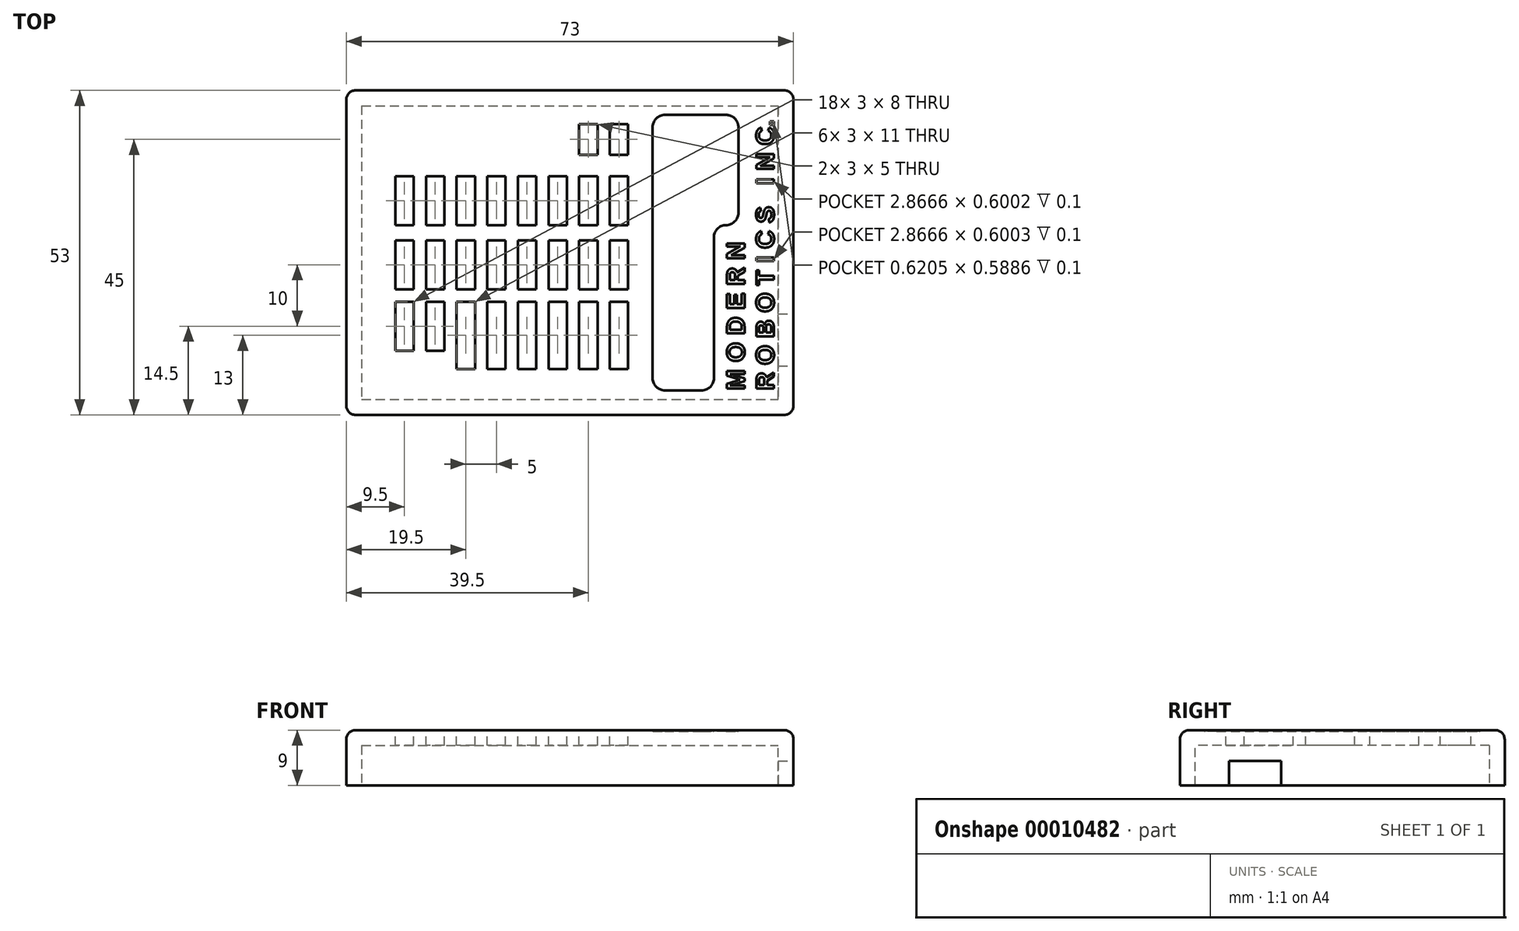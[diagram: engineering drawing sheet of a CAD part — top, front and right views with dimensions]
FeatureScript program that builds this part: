
annotation { "Feature Type Name" : "Feature", "Feature Type Description" : "" }
export const myFeature = defineFeature(function(context is Context, id is Id, definition is map)
    precondition{}
    {
        {
            var Q0;
            Q0=qCreatedBy(makeId("Top.planeOp"),FACE);
            var sketch = newSketch(context, id + "F0", { "sketchPlane" : qUnion([Q0])});
            skLineSegment(sketch, "E0.bottom", {"start": v(0, 0) * mm, "end": v(73, 0) * mm});
            skLineSegment(sketch, "E0.top", {"start": v(0, 53) * mm, "end": v(73, 53) * mm});
            skLineSegment(sketch, "E0.left", {"start": v(0, 0) * mm, "end": v(0, 53) * mm});
            skLineSegment(sketch, "E0.right", {"start": v(73, 0) * mm, "end": v(73, 53) * mm});
            skSolve(sketch);
        }
        {
            var Q0;
            Q0=qSketchRegion(id+"F0",true);
            extrude(context, id + "F1", {"entities" : qUnion([Q0]), "depth" : 9 * mm});
        }
        {
            var Q0;
            Q0=makeQuery(id+"F1.opExtrude","SWEPT_EDGE",EDGE,{"disambiguationData":[OSD([sQuery(id+"F0.wireOp",EDGE,"E0.bottom"),sQuery(id+"F0.wireOp",EDGE,"E0.left")])]});
            var Q1;
            Q1=makeQuery(id+"F1.opExtrude","CAP_EDGE",EDGE,{"disambiguationData":[OSD([sQuery(id+"F0.wireOp",EDGE,"E0.bottom")])],"isStart":false});
            var Q2;
            Q2=makeQuery(id+"F1.opExtrude","CAP_EDGE",EDGE,{"disambiguationData":[OSD([sQuery(id+"F0.wireOp",EDGE,"E0.left")])],"isStart":false});
            var Q3;
            Q3=makeQuery(id+"F1.opExtrude","SWEPT_EDGE",EDGE,{"disambiguationData":[OSD([sQuery(id+"F0.wireOp",EDGE,"E0.bottom"),sQuery(id+"F0.wireOp",EDGE,"E0.right")])]});
            var Q4;
            Q4=makeQuery(id+"F1.opExtrude","CAP_EDGE",EDGE,{"disambiguationData":[OSD([sQuery(id+"F0.wireOp",EDGE,"E0.right")])],"isStart":false});
            var Q5;
            Q5=makeQuery(id+"F1.opExtrude","CAP_EDGE",EDGE,{"disambiguationData":[OSD([sQuery(id+"F0.wireOp",EDGE,"E0.top")])],"isStart":false});
            var Q6;
            Q6=makeQuery(id+"F1.opExtrude","SWEPT_EDGE",EDGE,{"disambiguationData":[OSD([sQuery(id+"F0.wireOp",EDGE,"E0.top"),sQuery(id+"F0.wireOp",EDGE,"E0.right")])]});
            var Q7;
            Q7=makeQuery(id+"F1.opExtrude","SWEPT_EDGE",EDGE,{"disambiguationData":[OSD([sQuery(id+"F0.wireOp",EDGE,"E0.top"),sQuery(id+"F0.wireOp",EDGE,"E0.left")])]});
            fillet(context, id + "F2", {"entities" : qUnion([Q0, Q1, Q2, Q3, Q4, Q5, Q6, Q7]), "radius" : 1.5 * mm, "tangentPropagation" : true, "allowEdgeOverflow" : false});
        }
        {
            var Q0;
            Q0=makeQuery(id+"F1.opExtrude","CAP_FACE",FACE,{"disambiguationData":[OSD([sQuery(id+"F0.wireOp",EDGE,"E0.bottom"),sQuery(id+"F0.wireOp",EDGE,"E0.top"),sQuery(id+"F0.wireOp",EDGE,"E0.left"),sQuery(id+"F0.wireOp",EDGE,"E0.right")])],"isStart":true});
            shell(context, id + "F3", {"entities" : qUnion([Q0]), "thickness" : 2.5 * mm});
        }
        {
            var Q0;
            Q0=makeQuery(id+"F1.opExtrude","SWEPT_FACE",FACE,{"disambiguationData":[OSD([sQuery(id+"F0.wireOp",EDGE,"E0.right")])]});
            var sketch = newSketch(context, id + "F4", { "sketchPlane" : qUnion([Q0])});
            skLineSegment(sketch, "E1.bottom", {"start": v(8, 4) * mm, "end": v(16.5, 4) * mm});
            skLineSegment(sketch, "E1.top", {"start": v(8, 0) * mm, "end": v(16.5, 0) * mm});
            skLineSegment(sketch, "E1.left", {"start": v(8, 4) * mm, "end": v(8, 0) * mm});
            skLineSegment(sketch, "E1.right", {"start": v(16.5, 4) * mm, "end": v(16.5, 0) * mm});
            skPoint(sketch, "E2", {"position": v(16.97, -0.37) * mm});
            skPoint(sketch, "E3", {"position": v(100.9, 31.9) * mm});
            skSolve(sketch);
        }
        {
            var Q0;
            Q0=qSketchRegion(id+"F4",true);
            extrude(context, id + "F5", {"entities" : qUnion([Q0]), "operationType" : NewBodyOperationType.REMOVE, "endBound" : BoundingType.UP_TO_NEXT, "oppositeDirection" : true, "depth" : 25 * mm});
        }
        {
            var Q0;
            Q0=makeQuery(id+"F1.opExtrude","CAP_FACE",FACE,{"disambiguationData":[OSD([sQuery(id+"F0.wireOp",EDGE,"E0.bottom"),sQuery(id+"F0.wireOp",EDGE,"E0.top"),sQuery(id+"F0.wireOp",EDGE,"E0.left"),sQuery(id+"F0.wireOp",EDGE,"E0.right")])],"isStart":false});
            var sketch = newSketch(context, id + "F6", { "sketchPlane" : qUnion([Q0])});
            skText(sketch, "E4", { "text": "M O D E R N\nR O B O T I C S   I N C.", "fontName": "Arimo-Bold.ttf"});
            const initialGuessF6  = {"E4": [0.065, 0.004, 0, 1, 0.003]};
            skSetInitialGuess(sketch, initialGuessF6);
            skSolve(sketch);
        }
        {
            var Q0;
            Q0=qSketchRegion(id+"F6",true);
            extrude(context, id + "F7", {"entities" : qUnion([Q0]), "operationType" : NewBodyOperationType.REMOVE, "oppositeDirection" : true, "depth" : .1 * mm});
        }
        {
            var Q0;
            Q0=makeQuery(id+"F6.imprint","IMPRINT",FACE,{"disambiguationData":[TD([[makeQuery(id+"F6.imprint","IMPRINT",EDGE,{"derivedFrom":sQuery(id+"F6.wireOp",EDGE,"E4.sketch_text.stroke-0")}),1.0]])]});
            var sketch = newSketch(context, id + "F8", { "sketchPlane" : qUnion([Q0])});
            skLineSegment(sketch, "E5.bottom", {"start": v(8, 31) * mm, "end": v(11, 31) * mm});
            skLineSegment(sketch, "E5.top", {"start": v(8, 39) * mm, "end": v(11, 39) * mm});
            skLineSegment(sketch, "E5.left", {"start": v(8, 31) * mm, "end": v(8, 39) * mm});
            skLineSegment(sketch, "E5.right", {"start": v(11, 31) * mm, "end": v(11, 39) * mm});
            skLineSegment(sketch, "E6.0.1.0", {"start": v(8, 20.5) * mm, "end": v(8, 28.5) * mm});
            skLineSegment(sketch, "E6.0.1.1", {"start": v(11, 20.5) * mm, "end": v(11, 28.5) * mm});
            skLineSegment(sketch, "E6.0.1.2", {"start": v(8, 20.5) * mm, "end": v(11, 20.5) * mm});
            skLineSegment(sketch, "E6.0.1.3", {"start": v(8, 28.5) * mm, "end": v(11, 28.5) * mm});
            skLineSegment(sketch, "E6.1.0.0", {"start": v(13, 31) * mm, "end": v(13, 39) * mm});
            skLineSegment(sketch, "E6.1.0.1", {"start": v(16, 31) * mm, "end": v(16, 39) * mm});
            skLineSegment(sketch, "E6.1.0.2", {"start": v(13, 31) * mm, "end": v(16, 31) * mm});
            skLineSegment(sketch, "E6.1.0.3", {"start": v(13, 39) * mm, "end": v(16, 39) * mm});
            skLineSegment(sketch, "E6.1.1.0", {"start": v(13, 20.5) * mm, "end": v(13, 28.5) * mm});
            skLineSegment(sketch, "E6.1.1.1", {"start": v(16, 20.5) * mm, "end": v(16, 28.5) * mm});
            skLineSegment(sketch, "E6.1.1.2", {"start": v(13, 20.5) * mm, "end": v(16, 20.5) * mm});
            skLineSegment(sketch, "E6.1.1.3", {"start": v(13, 28.5) * mm, "end": v(16, 28.5) * mm});
            skLineSegment(sketch, "E6.2.0.0", {"start": v(18, 31) * mm, "end": v(18, 39) * mm});
            skLineSegment(sketch, "E6.2.0.1", {"start": v(21, 31) * mm, "end": v(21, 39) * mm});
            skLineSegment(sketch, "E6.2.0.2", {"start": v(18, 31) * mm, "end": v(21, 31) * mm});
            skLineSegment(sketch, "E6.2.0.3", {"start": v(18, 39) * mm, "end": v(21, 39) * mm});
            skLineSegment(sketch, "E6.2.1.0", {"start": v(18, 20.5) * mm, "end": v(18, 28.5) * mm});
            skLineSegment(sketch, "E6.2.1.1", {"start": v(21, 20.5) * mm, "end": v(21, 28.5) * mm});
            skLineSegment(sketch, "E6.2.1.2", {"start": v(18, 20.5) * mm, "end": v(21, 20.5) * mm});
            skLineSegment(sketch, "E6.2.1.3", {"start": v(18, 28.5) * mm, "end": v(21, 28.5) * mm});
            skLineSegment(sketch, "E6.3.0.0", {"start": v(23, 31) * mm, "end": v(23, 39) * mm});
            skLineSegment(sketch, "E6.3.0.1", {"start": v(26, 31) * mm, "end": v(26, 39) * mm});
            skLineSegment(sketch, "E6.3.0.2", {"start": v(23, 31) * mm, "end": v(26, 31) * mm});
            skLineSegment(sketch, "E6.3.0.3", {"start": v(23, 39) * mm, "end": v(26, 39) * mm});
            skLineSegment(sketch, "E6.3.1.0", {"start": v(23, 20.5) * mm, "end": v(23, 28.5) * mm});
            skLineSegment(sketch, "E6.3.1.1", {"start": v(26, 20.5) * mm, "end": v(26, 28.5) * mm});
            skLineSegment(sketch, "E6.3.1.2", {"start": v(23, 20.5) * mm, "end": v(26, 20.5) * mm});
            skLineSegment(sketch, "E6.3.1.3", {"start": v(23, 28.5) * mm, "end": v(26, 28.5) * mm});
            skLineSegment(sketch, "E6.4.0.0", {"start": v(28, 31) * mm, "end": v(28, 39) * mm});
            skLineSegment(sketch, "E6.4.0.1", {"start": v(31, 31) * mm, "end": v(31, 39) * mm});
            skLineSegment(sketch, "E6.4.0.2", {"start": v(28, 31) * mm, "end": v(31, 31) * mm});
            skLineSegment(sketch, "E6.4.0.3", {"start": v(28, 39) * mm, "end": v(31, 39) * mm});
            skLineSegment(sketch, "E6.4.1.0", {"start": v(28, 20.5) * mm, "end": v(28, 28.5) * mm});
            skLineSegment(sketch, "E6.4.1.1", {"start": v(31, 20.5) * mm, "end": v(31, 28.5) * mm});
            skLineSegment(sketch, "E6.4.1.2", {"start": v(28, 20.5) * mm, "end": v(31, 20.5) * mm});
            skLineSegment(sketch, "E6.4.1.3", {"start": v(28, 28.5) * mm, "end": v(31, 28.5) * mm});
            skLineSegment(sketch, "E6.5.0.0", {"start": v(33, 31) * mm, "end": v(33, 39) * mm});
            skLineSegment(sketch, "E6.5.0.1", {"start": v(36, 31) * mm, "end": v(36, 39) * mm});
            skLineSegment(sketch, "E6.5.0.2", {"start": v(33, 31) * mm, "end": v(36, 31) * mm});
            skLineSegment(sketch, "E6.5.0.3", {"start": v(33, 39) * mm, "end": v(36, 39) * mm});
            skLineSegment(sketch, "E6.5.1.0", {"start": v(33, 20.5) * mm, "end": v(33, 28.5) * mm});
            skLineSegment(sketch, "E6.5.1.1", {"start": v(36, 20.5) * mm, "end": v(36, 28.5) * mm});
            skLineSegment(sketch, "E6.5.1.2", {"start": v(33, 20.5) * mm, "end": v(36, 20.5) * mm});
            skLineSegment(sketch, "E6.5.1.3", {"start": v(33, 28.5) * mm, "end": v(36, 28.5) * mm});
            skLineSegment(sketch, "E6.6.0.0", {"start": v(38, 31) * mm, "end": v(38, 39) * mm});
            skLineSegment(sketch, "E6.6.0.1", {"start": v(41, 31) * mm, "end": v(41, 39) * mm});
            skLineSegment(sketch, "E6.6.0.2", {"start": v(38, 31) * mm, "end": v(41, 31) * mm});
            skLineSegment(sketch, "E6.6.0.3", {"start": v(38, 39) * mm, "end": v(41, 39) * mm});
            skLineSegment(sketch, "E6.6.1.0", {"start": v(38, 20.5) * mm, "end": v(38, 28.5) * mm});
            skLineSegment(sketch, "E6.6.1.1", {"start": v(41, 20.5) * mm, "end": v(41, 28.5) * mm});
            skLineSegment(sketch, "E6.6.1.2", {"start": v(38, 20.5) * mm, "end": v(41, 20.5) * mm});
            skLineSegment(sketch, "E6.6.1.3", {"start": v(38, 28.5) * mm, "end": v(41, 28.5) * mm});
            skLineSegment(sketch, "E6.7.0.0", {"start": v(43, 31) * mm, "end": v(43, 39) * mm});
            skLineSegment(sketch, "E6.7.0.1", {"start": v(46, 31) * mm, "end": v(46, 39) * mm});
            skLineSegment(sketch, "E6.7.0.2", {"start": v(43, 31) * mm, "end": v(46, 31) * mm});
            skLineSegment(sketch, "E6.7.0.3", {"start": v(43, 39) * mm, "end": v(46, 39) * mm});
            skLineSegment(sketch, "E6.7.1.0", {"start": v(43, 20.5) * mm, "end": v(43, 28.5) * mm});
            skLineSegment(sketch, "E6.7.1.1", {"start": v(46, 20.5) * mm, "end": v(46, 28.5) * mm});
            skLineSegment(sketch, "E6.7.1.2", {"start": v(43, 20.5) * mm, "end": v(46, 20.5) * mm});
            skLineSegment(sketch, "E6.7.1.3", {"start": v(43, 28.5) * mm, "end": v(46, 28.5) * mm});
            skLineSegment(sketch, "E6.direction1", {"start": v(8, 31) * mm, "end": v(13, 31) * mm, "construction": true});
            skLineSegment(sketch, "E6.direction2", {"start": v(8, 31) * mm, "end": v(8, 20.5) * mm, "construction": true});
            skLineSegment(sketch, "E7.0.1.0", {"start": v(13, 10.5) * mm, "end": v(13, 18.5) * mm});
            skLineSegment(sketch, "E7.0.1.1", {"start": v(13, 18.5) * mm, "end": v(16, 18.5) * mm});
            skLineSegment(sketch, "E7.0.1.2", {"start": v(16, 10.5) * mm, "end": v(16, 18.5) * mm});
            skLineSegment(sketch, "E7.0.1.3", {"start": v(13, 10.5) * mm, "end": v(16, 10.5) * mm});
            skLineSegment(sketch, "E7.0.1.4", {"start": v(8, 10.5) * mm, "end": v(11, 10.5) * mm});
            skLineSegment(sketch, "E7.0.1.5", {"start": v(8, 18.5) * mm, "end": v(11, 18.5) * mm});
            skLineSegment(sketch, "E7.0.1.6", {"start": v(8, 10.5) * mm, "end": v(8, 18.5) * mm});
            skLineSegment(sketch, "E7.0.1.7", {"start": v(11, 10.5) * mm, "end": v(11, 18.5) * mm});
            skLineSegment(sketch, "E7.0.1.8", {"start": v(8, 21) * mm, "end": v(8, 10.5) * mm, "construction": true});
            skLineSegment(sketch, "E7.direction1", {"start": v(13, 20.5) * mm, "end": v(15.38, 20.5) * mm, "construction": true});
            skLineSegment(sketch, "E7.direction2", {"start": v(13, 20.5) * mm, "end": v(13, 10.5) * mm, "construction": true});
            skLineSegment(sketch, "E8.bottom", {"start": v(18, 18.5) * mm, "end": v(21, 18.5) * mm});
            skLineSegment(sketch, "E8.top", {"start": v(18, 7.5) * mm, "end": v(21, 7.5) * mm});
            skLineSegment(sketch, "E8.left", {"start": v(18, 18.5) * mm, "end": v(18, 7.5) * mm});
            skLineSegment(sketch, "E8.right", {"start": v(21, 18.5) * mm, "end": v(21, 7.5) * mm});
            skLineSegment(sketch, "E9.1.0.0", {"start": v(26, 18.5) * mm, "end": v(26, 7.5) * mm});
            skLineSegment(sketch, "E9.1.0.1", {"start": v(23, 18.5) * mm, "end": v(23, 7.5) * mm});
            skLineSegment(sketch, "E9.1.0.2", {"start": v(23, 7.5) * mm, "end": v(26, 7.5) * mm});
            skLineSegment(sketch, "E9.1.0.3", {"start": v(23, 18.5) * mm, "end": v(26, 18.5) * mm});
            skLineSegment(sketch, "E9.2.0.0", {"start": v(31, 18.5) * mm, "end": v(31, 7.5) * mm});
            skLineSegment(sketch, "E9.2.0.1", {"start": v(28, 18.5) * mm, "end": v(28, 7.5) * mm});
            skLineSegment(sketch, "E9.2.0.2", {"start": v(28, 7.5) * mm, "end": v(31, 7.5) * mm});
            skLineSegment(sketch, "E9.2.0.3", {"start": v(28, 18.5) * mm, "end": v(31, 18.5) * mm});
            skLineSegment(sketch, "E9.3.0.0", {"start": v(36, 18.5) * mm, "end": v(36, 7.5) * mm});
            skLineSegment(sketch, "E9.3.0.1", {"start": v(33, 18.5) * mm, "end": v(33, 7.5) * mm});
            skLineSegment(sketch, "E9.3.0.2", {"start": v(33, 7.5) * mm, "end": v(36, 7.5) * mm});
            skLineSegment(sketch, "E9.3.0.3", {"start": v(33, 18.5) * mm, "end": v(36, 18.5) * mm});
            skLineSegment(sketch, "E9.4.0.0", {"start": v(41, 18.5) * mm, "end": v(41, 7.5) * mm});
            skLineSegment(sketch, "E9.4.0.1", {"start": v(38, 18.5) * mm, "end": v(38, 7.5) * mm});
            skLineSegment(sketch, "E9.4.0.2", {"start": v(38, 7.5) * mm, "end": v(41, 7.5) * mm});
            skLineSegment(sketch, "E9.4.0.3", {"start": v(38, 18.5) * mm, "end": v(41, 18.5) * mm});
            skLineSegment(sketch, "E9.5.0.0", {"start": v(46, 18.5) * mm, "end": v(46, 7.5) * mm});
            skLineSegment(sketch, "E9.5.0.1", {"start": v(43, 18.5) * mm, "end": v(43, 7.5) * mm});
            skLineSegment(sketch, "E9.5.0.2", {"start": v(43, 7.5) * mm, "end": v(46, 7.5) * mm});
            skLineSegment(sketch, "E9.5.0.3", {"start": v(43, 18.5) * mm, "end": v(46, 18.5) * mm});
            skLineSegment(sketch, "E9.direction1", {"start": v(21, 7.5) * mm, "end": v(26, 7.5) * mm, "construction": true});
            skLineSegment(sketch, "E10.bottom", {"start": v(46, 42.5) * mm, "end": v(43, 42.5) * mm});
            skLineSegment(sketch, "E10.top", {"start": v(46, 47.5) * mm, "end": v(43, 47.5) * mm});
            skLineSegment(sketch, "E10.left", {"start": v(46, 42.5) * mm, "end": v(46, 47.5) * mm});
            skLineSegment(sketch, "E10.right", {"start": v(43, 42.5) * mm, "end": v(43, 47.5) * mm});
            skLineSegment(sketch, "E11.1.0.0", {"start": v(41, 42.5) * mm, "end": v(38, 42.5) * mm});
            skLineSegment(sketch, "E11.1.0.1", {"start": v(41, 42.5) * mm, "end": v(41, 47.5) * mm});
            skLineSegment(sketch, "E11.1.0.2", {"start": v(38, 42.5) * mm, "end": v(38, 47.5) * mm});
            skLineSegment(sketch, "E11.1.0.3", {"start": v(41, 47.5) * mm, "end": v(38, 47.5) * mm});
            skLineSegment(sketch, "E11.direction1", {"start": v(43, 42.5) * mm, "end": v(38, 42.5) * mm, "construction": true});
            skSolve(sketch);
        }
        {
            var Q0;
            Q0 = qSketchRegion(id + "F8", true);
            extrude(context, id + "F9", {"entities" : qUnion([Q0]), "operationType" : NewBodyOperationType.REMOVE, "endBound" : BoundingType.UP_TO_NEXT, "oppositeDirection" : true, "depth" : 25 * mm});
        }
        {
            var Q0;
            {var subQ0=sQuery(id+"F0.wireOp",EDGE,"E0.bottom");var subQ1=sQuery(id+"F0.wireOp",EDGE,"E0.top");var subQ2=sQuery(id+"F0.wireOp",EDGE,"E0.left");var subQ3=sQuery(id+"F0.wireOp",EDGE,"E0.right");Q0=makeQuery(id+"F7.boolean.opBoolean","SPLIT",FACE,{"disambiguationData":[TD([makeQuery(id+"F2.opFillet","BLEND_FACE",FACE,{"disambiguationData":[OSD([subQ0])]})])],"derivedFrom":makeQuery(id+"F1.opExtrude","CAP_FACE",FACE,{"disambiguationData":[OSD([subQ0,subQ1,subQ2,subQ3])],"isStart":false})});}
            var sketch = newSketch(context, id + "F10", { "sketchPlane" : qUnion([Q0])});
            skLineSegment(sketch, "E12.bottom", {"start": v(52, 4) * mm, "end": v(58, 4) * mm});
            skLineSegment(sketch, "E12.left", {"start": v(50, 6) * mm, "end": v(50, 47) * mm});
            skLineSegment(sketch, "E12.right", {"start": v(60, 6) * mm, "end": v(60, 29) * mm});
            skLineSegment(sketch, "E13.top", {"start": v(62, 31) * mm, "end": v(62, 31) * mm});
            skLineSegment(sketch, "E14", {"start": v(64, 33) * mm, "end": v(64, 47) * mm});
            skLineSegment(sketch, "E15", {"start": v(62, 49) * mm, "end": v(52, 49) * mm});
            skPoint(sketch, "E16.visualSharp", {"position": v(50, 4) * mm});
            skArc(sketch, "E16.filletArc", {"start": v(50, 6) * mm, "mid": v(50.59, 4.59) * mm, "end": v(52, 4) * mm});
            skPoint(sketch, "E17.visualSharp", {"position": v(60, 4) * mm});
            skArc(sketch, "E17.filletArc", {"start": v(58, 4) * mm, "mid": v(59.41, 4.59) * mm, "end": v(60, 6) * mm});
            skPoint(sketch, "E18.visualSharp", {"position": v(60, 31) * mm});
            skArc(sketch, "E18.filletArc", {"start": v(62, 31) * mm, "mid": v(60.59, 30.41) * mm, "end": v(60, 29) * mm});
            skPoint(sketch, "E19.visualSharp", {"position": v(64, 49) * mm});
            skArc(sketch, "E19.filletArc", {"start": v(64, 47) * mm, "mid": v(63.41, 48.41) * mm, "end": v(62, 49) * mm});
            skPoint(sketch, "E20.visualSharp", {"position": v(64, 31) * mm});
            skArc(sketch, "E20.filletArc", {"start": v(62, 31) * mm, "mid": v(63.41, 31.59) * mm, "end": v(64, 33) * mm});
            skPoint(sketch, "E21.newPointB", {"position": v(50, 49) * mm});
            skArc(sketch, "E21.filletArc", {"start": v(52, 49) * mm, "mid": v(50.59, 48.4) * mm, "end": v(50, 47) * mm});
            skSolve(sketch);
        }
        {
            var Q0;
            Q0 = qSketchRegion(id + "F10", true);
            extrude(context, id + "F11", {"entities" : qUnion([Q0]), "operationType" : NewBodyOperationType.REMOVE, "oppositeDirection" : true, "depth" : .2 * mm});
        }
        {
            var Q0;
            Q0=makeQuery(id+"F11.boolean.opBoolean","COPY",FACE,{"derivedFrom":makeQuery(id+"F11.opExtrude","CAP_FACE",FACE,{"disambiguationData":[OSD([sQuery(id+"F10.wireOp",EDGE,"E12.bottom"),sQuery(id+"F10.wireOp",EDGE,"E12.left"),sQuery(id+"F10.wireOp",EDGE,"E12.right"),sQuery(id+"F10.wireOp",EDGE,"E14"),sQuery(id+"F10.wireOp",EDGE,"E15"),sQuery(id+"F10.wireOp",EDGE,"E16.filletArc"),sQuery(id+"F10.wireOp",EDGE,"E17.filletArc"),sQuery(id+"F10.wireOp",EDGE,"E18.filletArc"),sQuery(id+"F10.wireOp",EDGE,"E19.filletArc"),sQuery(id+"F10.wireOp",EDGE,"E20.filletArc"),sQuery(id+"F10.wireOp",EDGE,"E21.filletArc")])],"isStart":false})});
            var Q1;
            Q1=makeQuery(id+"F11.boolean.opBoolean","COPY",EDGE,{"derivedFrom":makeQuery(id+"F11.opExtrude","CAP_EDGE",EDGE,{"disambiguationData":[OSD([sQuery(id+"F10.wireOp",EDGE,"E12.left")])],"isStart":true})});
            var Q2;
            Q2=makeQuery(id+"F11.boolean.opBoolean","COPY",EDGE,{"derivedFrom":makeQuery(id+"F11.opExtrude","CAP_EDGE",EDGE,{"disambiguationData":[OSD([sQuery(id+"F10.wireOp",EDGE,"E19.filletArc")])],"isStart":true})});
            var Q3;
            Q3=makeQuery(id+"F11.boolean.opBoolean","COPY",EDGE,{"derivedFrom":makeQuery(id+"F11.opExtrude","CAP_EDGE",EDGE,{"disambiguationData":[OSD([sQuery(id+"F10.wireOp",EDGE,"E21.filletArc")])],"isStart":true})});
            var Q4;
            Q4=makeQuery(id+"F11.boolean.opBoolean","COPY",EDGE,{"derivedFrom":makeQuery(id+"F11.opExtrude","CAP_EDGE",EDGE,{"disambiguationData":[OSD([sQuery(id+"F10.wireOp",EDGE,"E15")])],"isStart":true})});
            var Q5;
            Q5=makeQuery(id+"F11.boolean.opBoolean","COPY",EDGE,{"derivedFrom":makeQuery(id+"F11.opExtrude","CAP_EDGE",EDGE,{"disambiguationData":[OSD([sQuery(id+"F10.wireOp",EDGE,"E21.filletArc")])],"isStart":false})});
            var Q6;
            Q6=makeQuery(id+"F11.boolean.opBoolean","COPY",EDGE,{"derivedFrom":makeQuery(id+"F11.opExtrude","CAP_EDGE",EDGE,{"disambiguationData":[OSD([sQuery(id+"F10.wireOp",EDGE,"E19.filletArc")])],"isStart":false})});
            var Q7;
            Q7=makeQuery(id+"F11.boolean.opBoolean","COPY",EDGE,{"derivedFrom":makeQuery(id+"F11.opExtrude","CAP_EDGE",EDGE,{"disambiguationData":[OSD([sQuery(id+"F10.wireOp",EDGE,"E15")])],"isStart":false})});
            var Q8;
            Q8=makeQuery(id+"F11.boolean.opBoolean","COPY",EDGE,{"derivedFrom":makeQuery(id+"F11.opExtrude","CAP_EDGE",EDGE,{"disambiguationData":[OSD([sQuery(id+"F10.wireOp",EDGE,"E20.filletArc")])],"isStart":true})});
            var Q9;
            Q9=makeQuery(id+"F11.boolean.opBoolean","COPY",EDGE,{"derivedFrom":makeQuery(id+"F11.opExtrude","CAP_EDGE",EDGE,{"disambiguationData":[OSD([sQuery(id+"F10.wireOp",EDGE,"E14")])],"isStart":true})});
            var Q10;
            Q10=makeQuery(id+"F11.boolean.opBoolean","COPY",EDGE,{"derivedFrom":makeQuery(id+"F11.opExtrude","CAP_EDGE",EDGE,{"disambiguationData":[OSD([sQuery(id+"F10.wireOp",EDGE,"E20.filletArc")])],"isStart":false})});
            var Q11;
            Q11=makeQuery(id+"F11.boolean.opBoolean","COPY",EDGE,{"derivedFrom":makeQuery(id+"F11.opExtrude","CAP_EDGE",EDGE,{"disambiguationData":[OSD([sQuery(id+"F10.wireOp",EDGE,"E14")])],"isStart":false})});
            var Q12;
            Q12=makeQuery(id+"F11.boolean.opBoolean","COPY",EDGE,{"derivedFrom":makeQuery(id+"F11.opExtrude","CAP_EDGE",EDGE,{"disambiguationData":[OSD([sQuery(id+"F10.wireOp",EDGE,"E18.filletArc")])],"isStart":true})});
            var Q13;
            Q13=makeQuery(id+"F11.boolean.opBoolean","COPY",EDGE,{"derivedFrom":makeQuery(id+"F11.opExtrude","CAP_EDGE",EDGE,{"disambiguationData":[OSD([sQuery(id+"F10.wireOp",EDGE,"E18.filletArc")])],"isStart":false})});
            var Q14;
            Q14=makeQuery(id+"F11.boolean.opBoolean","COPY",EDGE,{"derivedFrom":makeQuery(id+"F11.opExtrude","CAP_EDGE",EDGE,{"disambiguationData":[OSD([sQuery(id+"F10.wireOp",EDGE,"E12.right")])],"isStart":true})});
            var Q15;
            Q15=makeQuery(id+"F11.boolean.opBoolean","COPY",EDGE,{"derivedFrom":makeQuery(id+"F11.opExtrude","CAP_EDGE",EDGE,{"disambiguationData":[OSD([sQuery(id+"F10.wireOp",EDGE,"E12.right")])],"isStart":false})});
            var Q16;
            Q16=makeQuery(id+"F11.boolean.opBoolean","COPY",EDGE,{"derivedFrom":makeQuery(id+"F11.opExtrude","CAP_EDGE",EDGE,{"disambiguationData":[OSD([sQuery(id+"F10.wireOp",EDGE,"E16.filletArc")])],"isStart":true})});
            var Q17;
            Q17=makeQuery(id+"F11.boolean.opBoolean","COPY",EDGE,{"derivedFrom":makeQuery(id+"F11.opExtrude","CAP_EDGE",EDGE,{"disambiguationData":[OSD([sQuery(id+"F10.wireOp",EDGE,"E17.filletArc")])],"isStart":true})});
            var Q18;
            Q18=makeQuery(id+"F11.boolean.opBoolean","COPY",EDGE,{"derivedFrom":makeQuery(id+"F11.opExtrude","CAP_EDGE",EDGE,{"disambiguationData":[OSD([sQuery(id+"F10.wireOp",EDGE,"E12.bottom")])],"isStart":true})});
            var Q19;
            Q19=makeQuery(id+"F11.boolean.opBoolean","COPY",EDGE,{"derivedFrom":makeQuery(id+"F11.opExtrude","CAP_EDGE",EDGE,{"disambiguationData":[OSD([sQuery(id+"F10.wireOp",EDGE,"E12.bottom")])],"isStart":false})});
            var Q20;
            Q20=makeQuery(id+"F11.boolean.opBoolean","COPY",EDGE,{"derivedFrom":makeQuery(id+"F11.opExtrude","CAP_EDGE",EDGE,{"disambiguationData":[OSD([sQuery(id+"F10.wireOp",EDGE,"E16.filletArc")])],"isStart":false})});
            var Q21;
            Q21=makeQuery(id+"F11.boolean.opBoolean","COPY",EDGE,{"derivedFrom":makeQuery(id+"F11.opExtrude","CAP_EDGE",EDGE,{"disambiguationData":[OSD([sQuery(id+"F10.wireOp",EDGE,"E17.filletArc")])],"isStart":false})});
            fillet(context, id + "F12", {"entities" : qUnion([Q0, Q1, Q2, Q3, Q4, Q5, Q6, Q7, Q8, Q9, Q10, Q11, Q12, Q13, Q14, Q15, Q16, Q17, Q18, Q19, Q20, Q21]), "radius" : .1 * mm, "tangentPropagation" : true, "allowEdgeOverflow" : false});
        }
    });
